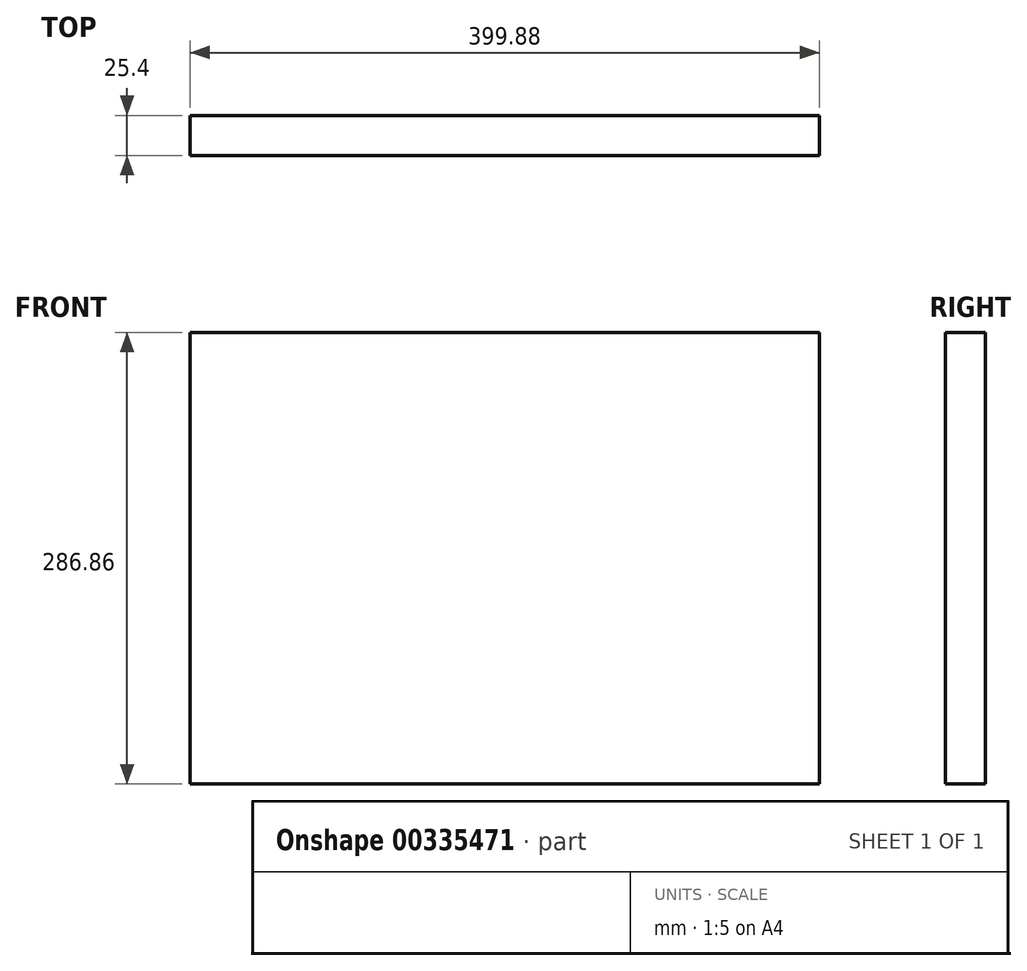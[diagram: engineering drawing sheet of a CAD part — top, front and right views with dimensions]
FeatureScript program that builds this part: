
annotation { "Feature Type Name" : "Feature", "Feature Type Description" : "" }
export const myFeature = defineFeature(function(context is Context, id is Id, definition is map)
    precondition{}
    {
        {
            var Q0;
            Q0=qCreatedBy(makeId("Front.planeOp"),FACE);
            var sketch = newSketch(context, id + "F0", { "sketchPlane" : qUnion([Q0])});
            skLineSegment(sketch, "E0.bottom", {"start": v(-156, -80.71) * mm, "end": v(243.88, -80.71) * mm});
            skLineSegment(sketch, "E0.top", {"start": v(-156, 206.15) * mm, "end": v(243.88, 206.15) * mm});
            skLineSegment(sketch, "E0.left", {"start": v(-156, -80.71) * mm, "end": v(-156, 206.15) * mm});
            skLineSegment(sketch, "E0.right", {"start": v(243.88, -80.71) * mm, "end": v(243.88, 206.15) * mm});
            skSolve(sketch);
        }
        {
            var Q0;
            Q0 = qSketchRegion(id + "F0", true);
            extrude(context, id + "F1", {"entities" : qUnion([Q0]), "depth" : 25.4 * mm});
        }
    });
